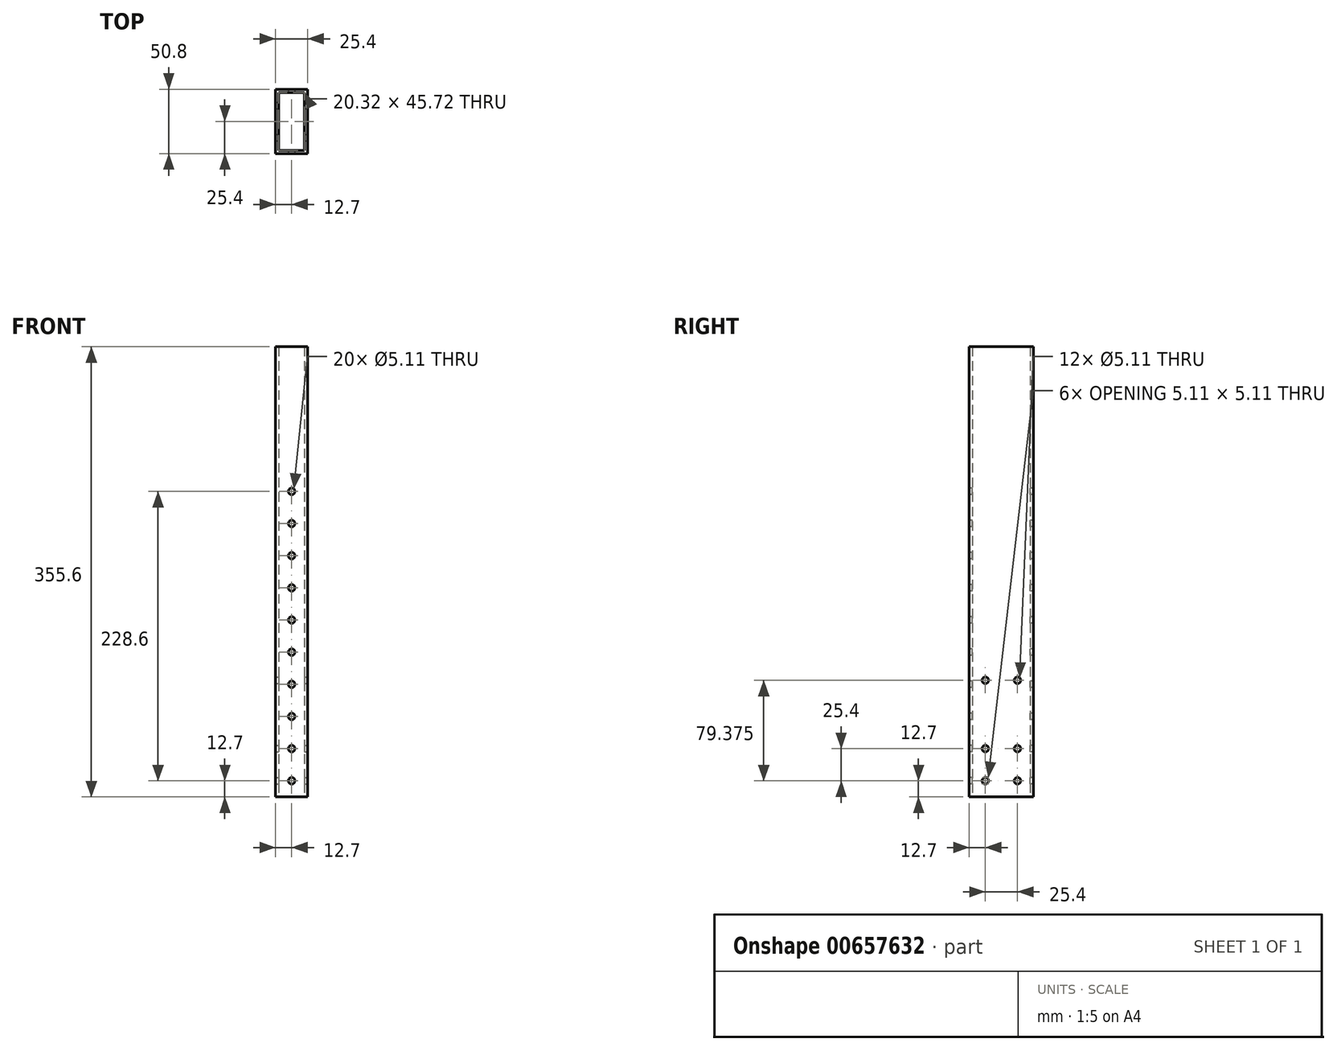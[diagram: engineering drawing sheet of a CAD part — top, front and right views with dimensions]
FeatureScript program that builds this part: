
annotation { "Feature Type Name" : "Feature", "Feature Type Description" : "" }
export const myFeature = defineFeature(function(context is Context, id is Id, definition is map)
    precondition{}
    {
        {
            var Q0;
            Q0=qCreatedBy(makeId("Top.planeOp"),FACE);
            var sketch = newSketch(context, id + "F0", { "sketchPlane" : qUnion([Q0])});
            skLineSegment(sketch, "E0.bottom", {"start": v(0, 0) * mm, "end": v(25.4, 0) * mm});
            skLineSegment(sketch, "E0.top", {"start": v(0, -50.8) * mm, "end": v(25.4, -50.8) * mm});
            skLineSegment(sketch, "E0.left", {"start": v(0, 0) * mm, "end": v(0, -50.8) * mm});
            skLineSegment(sketch, "E0.right", {"start": v(25.4, 0) * mm, "end": v(25.4, -50.8) * mm});
            skLineSegment(sketch, "E1.bottom", {"start": v(22.86, -48.26) * mm, "end": v(2.54, -48.26) * mm});
            skLineSegment(sketch, "E1.top", {"start": v(22.86, -2.54) * mm, "end": v(2.54, -2.54) * mm});
            skLineSegment(sketch, "E1.left", {"start": v(22.86, -48.26) * mm, "end": v(22.86, -2.54) * mm});
            skLineSegment(sketch, "E1.right", {"start": v(2.54, -48.26) * mm, "end": v(2.54, -2.54) * mm});
            skSolve(sketch);
        }
        {
            var Q0;
            Q0=makeQuery(id+"F0.imprint","IMPRINT",FACE,{"disambiguationData":[TD([[makeQuery(id+"F0.imprint","IMPRINT",EDGE,{"derivedFrom":sQuery(id+"F0.wireOp",EDGE,"E0.bottom")}),-1.0]])]});
            extrude(context, id + "F1", {"entities" : qUnion([Q0]), "depth" : 355.6 * mm, "offsetDistance" : 25.4 * mm});
        }
        {
            var Q0;
            Q0=makeQuery(id+"F1.opExtrude","SWEPT_FACE",FACE,{"disambiguationData":[OSD([sQuery(id+"F0.wireOp",EDGE,"E0.top")])]});
            var sketch = newSketch(context, id + "F2", { "sketchPlane" : qUnion([Q0])});
            skCircle(sketch, "E2", {"center": v(12.7, 12.7) * mm, "radius": 2.55 * mm});
            skCircle(sketch, "E3.0.1.0", {"center": v(12.7, 38.1) * mm, "radius": 2.55 * mm});
            skCircle(sketch, "E3.0.2.0", {"center": v(12.7, 63.5) * mm, "radius": 2.55 * mm});
            skCircle(sketch, "E3.0.3.0", {"center": v(12.7, 88.9) * mm, "radius": 2.55 * mm});
            skCircle(sketch, "E3.0.4.0", {"center": v(12.7, 114.3) * mm, "radius": 2.55 * mm});
            skCircle(sketch, "E3.0.5.0", {"center": v(12.7, 139.7) * mm, "radius": 2.55 * mm});
            skLineSegment(sketch, "E3.direction1", {"start": v(12.7, 12.7) * mm, "end": v(38.1, 12.7) * mm, "construction": true});
            skLineSegment(sketch, "E3.direction2", {"start": v(12.7, 12.7) * mm, "end": v(12.7, 38.1) * mm, "construction": true});
            skCircle(sketch, "E4.0.0.6", {"center": v(12.7, 165.1) * mm, "radius": 2.55 * mm});
            skCircle(sketch, "E4.0.0.7", {"center": v(12.7, 190.5) * mm, "radius": 2.55 * mm});
            skCircle(sketch, "E4.0.0.8", {"center": v(12.7, 215.9) * mm, "radius": 2.55 * mm});
            skCircle(sketch, "E5.0.0.9", {"center": v(12.7, 241.3) * mm, "radius": 2.55 * mm});
            skSolve(sketch);
        }
        {
            var Q0;
            Q0=makeQuery(id+"F2.imprint","IMPRINT",FACE,{"disambiguationData":[TD([[makeQuery(id+"F2.imprint","IMPRINT",EDGE,{"derivedFrom":sQuery(id+"F2.wireOp",EDGE,"E3.0.5.0")}),1.0]])]});
            var Q1;
            Q1=makeQuery(id+"F2.imprint","IMPRINT",FACE,{"disambiguationData":[TD([[makeQuery(id+"F2.imprint","IMPRINT",EDGE,{"derivedFrom":sQuery(id+"F2.wireOp",EDGE,"E3.0.4.0")}),1.0]])]});
            var Q2;
            Q2=makeQuery(id+"F2.imprint","IMPRINT",FACE,{"disambiguationData":[TD([[makeQuery(id+"F2.imprint","IMPRINT",EDGE,{"derivedFrom":sQuery(id+"F2.wireOp",EDGE,"E3.0.3.0")}),1.0]])]});
            var Q3;
            Q3=makeQuery(id+"F2.imprint","IMPRINT",FACE,{"disambiguationData":[TD([[makeQuery(id+"F2.imprint","IMPRINT",EDGE,{"derivedFrom":sQuery(id+"F2.wireOp",EDGE,"E3.0.2.0")}),1.0]])]});
            var Q4;
            Q4=makeQuery(id+"F2.imprint","IMPRINT",FACE,{"disambiguationData":[TD([[makeQuery(id+"F2.imprint","IMPRINT",EDGE,{"derivedFrom":sQuery(id+"F2.wireOp",EDGE,"E3.0.1.0")}),1.0]])]});
            var Q5;
            Q5=makeQuery(id+"F2.imprint","IMPRINT",FACE,{"disambiguationData":[TD([[makeQuery(id+"F2.imprint","IMPRINT",EDGE,{"derivedFrom":sQuery(id+"F2.wireOp",EDGE,"E2")}),1.0]])]});
            var Q6;
            Q6=makeQuery(id+"F2.imprint","IMPRINT",FACE,{"disambiguationData":[TD([[makeQuery(id+"F2.imprint","IMPRINT",EDGE,{"derivedFrom":sQuery(id+"F2.wireOp",EDGE,"E4.0.0.6")}),1.0]])]});
            var Q7;
            Q7=makeQuery(id+"F2.imprint","IMPRINT",FACE,{"disambiguationData":[TD([[makeQuery(id+"F2.imprint","IMPRINT",EDGE,{"derivedFrom":sQuery(id+"F2.wireOp",EDGE,"E4.0.0.7")}),1.0]])]});
            var Q8;
            Q8=makeQuery(id+"F2.imprint","IMPRINT",FACE,{"disambiguationData":[TD([[makeQuery(id+"F2.imprint","IMPRINT",EDGE,{"derivedFrom":sQuery(id+"F2.wireOp",EDGE,"E4.0.0.8")}),1.0]])]});
            var Q9;
            Q9=makeQuery(id+"F2.imprint","IMPRINT",FACE,{"disambiguationData":[TD([[makeQuery(id+"F2.imprint","IMPRINT",EDGE,{"derivedFrom":sQuery(id+"F2.wireOp",EDGE,"E5.0.0.9")}),1.0]])]});
            extrude(context, id + "F3", {"entities" : qUnion([Q0, Q1, Q2, Q3, Q4, Q5, Q6, Q7, Q8, Q9]), "operationType" : NewBodyOperationType.REMOVE, "oppositeDirection" : true, "depth" : 50.8 * mm, "offsetDistance" : 25.4 * mm});
        }
        {
            var Q0;
            Q0=makeQuery(id+"F1.opExtrude","SWEPT_FACE",FACE,{"disambiguationData":[OSD([sQuery(id+"F0.wireOp",EDGE,"E0.right")])]});
            var sketch = newSketch(context, id + "F4", { "sketchPlane" : qUnion([Q0])});
            skLineSegment(sketch, "E6.bottom", {"start": v(0, 0) * mm, "end": v(-50.8, 0) * mm});
            skLineSegment(sketch, "E6.top", {"start": v(0, 50.8) * mm, "end": v(-50.8, 50.8) * mm});
            skLineSegment(sketch, "E6.left", {"start": v(0, 0) * mm, "end": v(0, 50.8) * mm});
            skLineSegment(sketch, "E6.right", {"start": v(-50.8, 0) * mm, "end": v(-50.8, 50.8) * mm});
            skCircle(sketch, "E7", {"center": v(-38.1, 38.1) * mm, "radius": 2.55 * mm});
            skCircle(sketch, "E8.0.1.0", {"center": v(-38.1, 12.7) * mm, "radius": 2.55 * mm});
            skCircle(sketch, "E8.1.0.0", {"center": v(-12.7, 38.1) * mm, "radius": 2.55 * mm});
            skCircle(sketch, "E8.1.1.0", {"center": v(-12.7, 12.7) * mm, "radius": 2.55 * mm});
            skLineSegment(sketch, "E8.direction1", {"start": v(-38.1, 38.1) * mm, "end": v(-12.7, 38.1) * mm, "construction": true});
            skLineSegment(sketch, "E8.direction2", {"start": v(-38.1, 38.1) * mm, "end": v(-38.1, 12.7) * mm, "construction": true});
            skLineSegment(sketch, "E9", {"start": v(-50.8, 53.98) * mm, "end": v(0, 53.97) * mm});
            skCircle(sketch, "E10", {"center": v(-38.1, 92.08) * mm, "radius": 2.55 * mm});
            skCircle(sketch, "E11", {"center": v(-12.7, 92.07) * mm, "radius": 2.55 * mm});
            skSolve(sketch);
        }
        {
            var Q0;
            Q0=makeQuery(id+"F4.imprint","IMPRINT",FACE,{"disambiguationData":[TD([[makeQuery(id+"F4.imprint","IMPRINT",EDGE,{"derivedFrom":sQuery(id+"F4.wireOp",EDGE,"E7")}),1.0]])]});
            var Q1;
            Q1=makeQuery(id+"F4.imprint","IMPRINT",FACE,{"disambiguationData":[TD([[makeQuery(id+"F4.imprint","IMPRINT",EDGE,{"derivedFrom":sQuery(id+"F4.wireOp",EDGE,"E8.1.0.0")}),1.0]])]});
            var Q2;
            Q2=makeQuery(id+"F4.imprint","IMPRINT",FACE,{"disambiguationData":[TD([[makeQuery(id+"F4.imprint","IMPRINT",EDGE,{"derivedFrom":sQuery(id+"F4.wireOp",EDGE,"E8.1.1.0")}),1.0]])]});
            var Q3;
            Q3=makeQuery(id+"F4.imprint","IMPRINT",FACE,{"disambiguationData":[TD([[makeQuery(id+"F4.imprint","IMPRINT",EDGE,{"derivedFrom":sQuery(id+"F4.wireOp",EDGE,"E8.0.1.0")}),1.0]])]});
            var Q4;
            Q4=makeQuery(id+"F4.imprint","IMPRINT",FACE,{"disambiguationData":[TD([[makeQuery(id+"F4.imprint","IMPRINT",EDGE,{"derivedFrom":sQuery(id+"F4.wireOp",EDGE,"E10")}),1.0]])]});
            var Q5;
            Q5=makeQuery(id+"F4.imprint","IMPRINT",FACE,{"disambiguationData":[TD([[makeQuery(id+"F4.imprint","IMPRINT",EDGE,{"derivedFrom":sQuery(id+"F4.wireOp",EDGE,"E11")}),1.0]])]});
            extrude(context, id + "F5", {"entities" : qUnion([Q0, Q1, Q2, Q3, Q4, Q5]), "operationType" : NewBodyOperationType.REMOVE, "oppositeDirection" : true, "depth" : 25.4 * mm, "offsetDistance" : 25.4 * mm});
        }
    });
